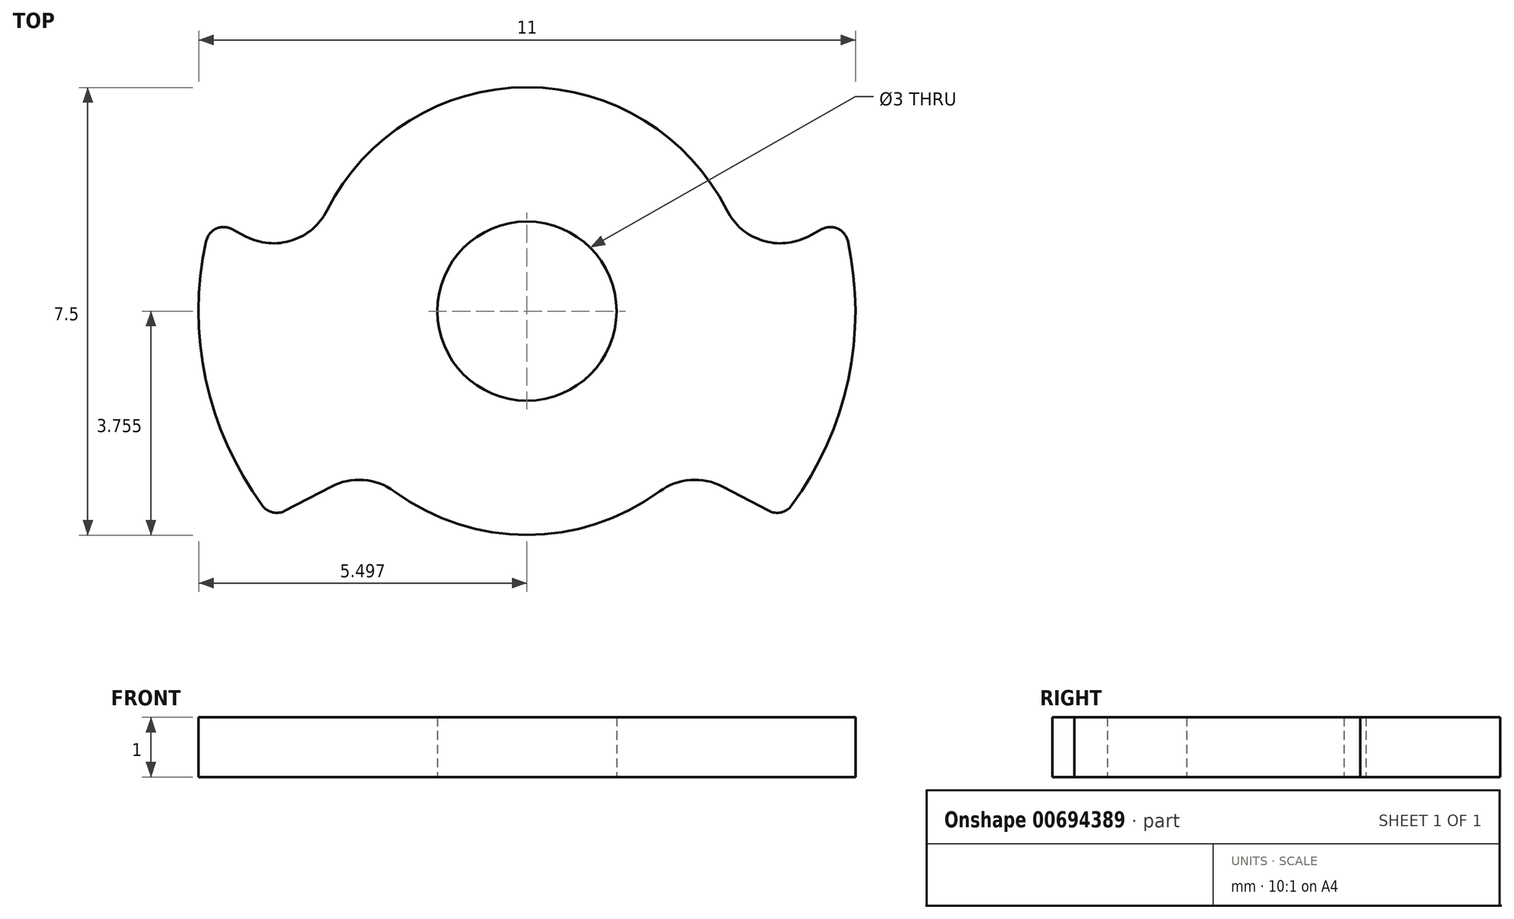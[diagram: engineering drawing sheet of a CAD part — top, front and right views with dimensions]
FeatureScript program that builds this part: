
annotation { "Feature Type Name" : "Feature", "Feature Type Description" : "" }
export const myFeature = defineFeature(function(context is Context, id is Id, definition is map)
    precondition{}
    {
        {
            var Q0;
            Q0=qCreatedBy(makeId("Top.planeOp"),FACE);
            var sketch = newSketch(context, id + "F0", { "sketchPlane" : qUnion([Q0])});
            skCircle(sketch, "E0", {"center": v(19.26, 32.5) * mm, "radius": 1.5 * mm});
            skArc(sketch, "E1", {"start": v(13.88, 33.68) * mm, "mid": v(13.88, 31.36) * mm, "end": v(14.83, 29.25) * mm});
            skArc(sketch, "E2", {"start": v(17.03, 29.48) * mm, "mid": v(19.26, 28.75) * mm, "end": v(21.48, 29.48) * mm});
            skArc(sketch, "E3.trimOffspring", {"start": v(23.69, 29.25) * mm, "mid": v(24.64, 31.36) * mm, "end": v(24.63, 33.68) * mm});
            skLineSegment(sketch, "E4", {"start": v(14.32, 33.88) * mm, "end": v(14.55, 33.76) * mm});
            skLineSegment(sketch, "E5", {"start": v(15.2, 29.16) * mm, "end": v(15.98, 29.56) * mm});
            skLineSegment(sketch, "E6.trimOffspring", {"start": v(22.54, 29.56) * mm, "end": v(23.3, 29.16) * mm});
            skLineSegment(sketch, "E7.trimOffspring", {"start": v(23.96, 33.76) * mm, "end": v(24.2, 33.88) * mm});
            skPoint(sketch, "E8.visualSharp", {"position": v(13.98, 34.05) * mm});
            skArc(sketch, "E8.filletArc", {"start": v(14.32, 33.88) * mm, "mid": v(14.05, 33.88) * mm, "end": v(13.88, 33.68) * mm});
            skPoint(sketch, "E9.visualSharp", {"position": v(14.98, 29.04) * mm});
            skArc(sketch, "E9.filletArc", {"start": v(14.83, 29.25) * mm, "mid": v(15, 29.13) * mm, "end": v(15.2, 29.16) * mm});
            skPoint(sketch, "E10.visualSharp", {"position": v(23.53, 29.04) * mm});
            skArc(sketch, "E10.filletArc", {"start": v(23.3, 29.16) * mm, "mid": v(23.51, 29.13) * mm, "end": v(23.69, 29.25) * mm});
            skPoint(sketch, "E11.visualSharp", {"position": v(24.53, 34.05) * mm});
            skArc(sketch, "E11.filletArc", {"start": v(24.63, 33.68) * mm, "mid": v(24.46, 33.88) * mm, "end": v(24.2, 33.88) * mm});
            skArc(sketch, "E12.trimOffspring", {"start": v(22.6, 34.2) * mm, "mid": v(19.26, 36.25) * mm, "end": v(15.9, 34.2) * mm});
            skPoint(sketch, "E13.visualSharp", {"position": v(15.58, 33.22) * mm});
            skArc(sketch, "E13.filletArc", {"start": v(14.55, 33.76) * mm, "mid": v(15.32, 33.69) * mm, "end": v(15.9, 34.2) * mm});
            skPoint(sketch, "E14.visualSharp", {"position": v(16.58, 29.88) * mm});
            skArc(sketch, "E14.filletArc", {"start": v(17.03, 29.48) * mm, "mid": v(16.52, 29.68) * mm, "end": v(15.98, 29.56) * mm});
            skPoint(sketch, "E15.visualSharp", {"position": v(21.94, 29.88) * mm});
            skArc(sketch, "E15.filletArc", {"start": v(22.54, 29.56) * mm, "mid": v(22, 29.68) * mm, "end": v(21.48, 29.48) * mm});
            skPoint(sketch, "E16.visualSharp", {"position": v(22.94, 33.22) * mm});
            skArc(sketch, "E16.filletArc", {"start": v(22.6, 34.2) * mm, "mid": v(23.2, 33.69) * mm, "end": v(23.96, 33.76) * mm});
            skSolve(sketch);
        }
        {
            var Q0;
            Q0=makeQuery(id+"F0.imprint","IMPRINT",FACE,{"disambiguationData":[TD([[makeQuery(id+"F0.imprint","IMPRINT",EDGE,{"derivedFrom":sQuery(id+"F0.wireOp",EDGE,"E0")}),-1.0]])]});
            extrude(context, id + "F1", {"entities" : qUnion([Q0]), "depth" : 1 * mm, "offsetDistance" : 25 * mm});
        }
    });
